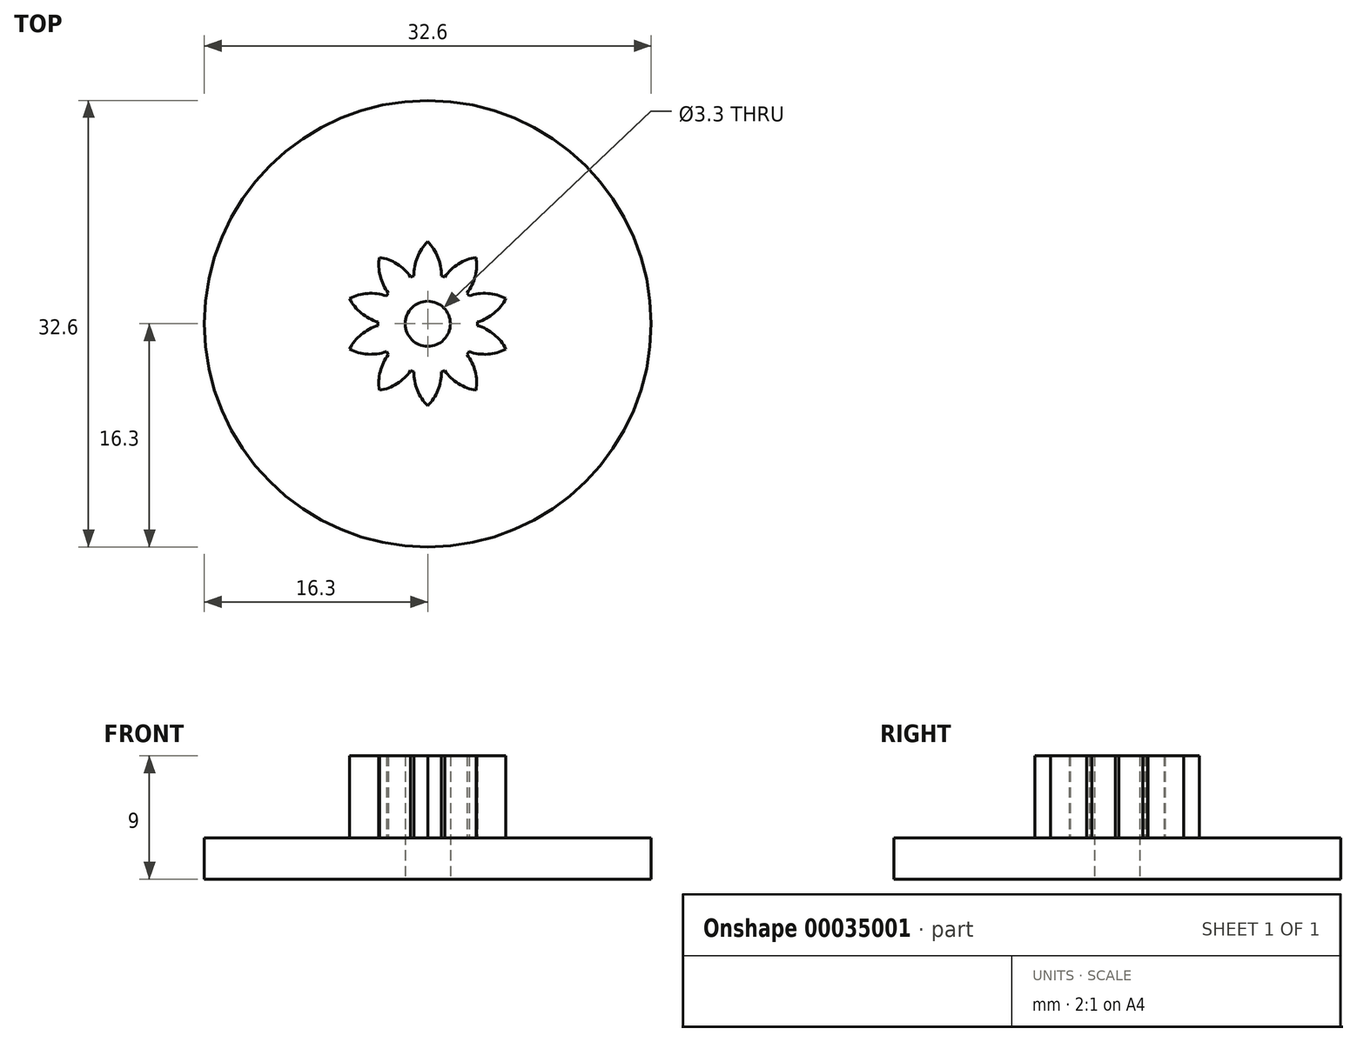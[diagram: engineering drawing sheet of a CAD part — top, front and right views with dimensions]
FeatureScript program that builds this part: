
annotation { "Feature Type Name" : "Feature", "Feature Type Description" : "" }
export const myFeature = defineFeature(function(context is Context, id is Id, definition is map)
    precondition{}
    {
        {
            var Q0;
            Q0=qCreatedBy(makeId("Top.planeOp"),FACE);
            var sketch = newSketch(context, id + "F0", { "sketchPlane" : qUnion([Q0])});
            skArc(sketch, "E0.62.0", {"start": v(9.16, 14.8) * mm, "mid": v(9.2, 14.18) * mm, "end": v(9, 13.59) * mm});
            skArc(sketch, "E0.62.3", {"start": v(9.16, 14.8) * mm, "mid": v(8.6, 14.55) * mm, "end": v(8.15, 14.12) * mm});
            skCircle(sketch, "E1", {"center": v(0, 0) * mm, "radius": 16.3 * mm});
            skPoint(sketch, "E2.center", {"position": v(-0.1, -0.17) * mm});
            skCircle(sketch, "E3", {"center": v(0, 0) * mm, "radius": 1.65 * mm});
            skPoint(sketch, "E4.center", {"position": v(-0.03, -0.04) * mm});
            skPoint(sketch, "E5.center", {"position": v(-0.02, -0.03) * mm});
            skArc(sketch, "E6.1.0", {"start": v(7.74, 15.58) * mm, "mid": v(7.84, 14.97) * mm, "end": v(7.7, 14.37) * mm});
            skArc(sketch, "E6.1.1", {"start": v(7.74, 15.58) * mm, "mid": v(7.2, 15.29) * mm, "end": v(6.8, 14.81) * mm});
            skArc(sketch, "E6.2.0", {"start": v(6.26, 16.23) * mm, "mid": v(6.4, 15.63) * mm, "end": v(6.33, 15.02) * mm});
            skArc(sketch, "E6.2.1", {"start": v(6.26, 16.23) * mm, "mid": v(5.74, 15.89) * mm, "end": v(5.4, 15.38) * mm});
            skArc(sketch, "E6.3.0", {"start": v(4.72, 16.74) * mm, "mid": v(4.93, 16.16) * mm, "end": v(4.9, 15.54) * mm});
            skArc(sketch, "E6.3.1", {"start": v(4.72, 16.74) * mm, "mid": v(4.24, 16.35) * mm, "end": v(3.94, 15.81) * mm});
            skArc(sketch, "E6.4.0", {"start": v(3.14, 17.1) * mm, "mid": v(3.4, 16.55) * mm, "end": v(3.43, 15.93) * mm});
            skArc(sketch, "E6.4.1", {"start": v(3.14, 17.1) * mm, "mid": v(2.7, 16.67) * mm, "end": v(2.45, 16.1) * mm});
            skArc(sketch, "E6.5.0", {"start": v(1.53, 17.32) * mm, "mid": v(1.84, 16.79) * mm, "end": v(1.93, 16.18) * mm});
            skArc(sketch, "E6.5.1", {"start": v(1.53, 17.32) * mm, "mid": v(1.13, 16.85) * mm, "end": v(0.94, 16.26) * mm});
            skArc(sketch, "E6.6.0", {"start": v(-0.09, 17.38) * mm, "mid": v(0.27, 16.88) * mm, "end": v(0.42, 16.28) * mm});
            skArc(sketch, "E6.6.1", {"start": v(-0.09, 17.38) * mm, "mid": v(-0.44, 16.88) * mm, "end": v(-0.58, 16.27) * mm});
            skArc(sketch, "E6.7.0", {"start": v(-1.7, 17.3) * mm, "mid": v(-1.3, 16.83) * mm, "end": v(-1.1, 16.24) * mm});
            skArc(sketch, "E6.7.1", {"start": v(-1.7, 17.3) * mm, "mid": v(-2.01, 16.76) * mm, "end": v(-2.1, 16.14) * mm});
            skArc(sketch, "E6.8.0", {"start": v(-3.31, 17.05) * mm, "mid": v(-2.87, 16.63) * mm, "end": v(-2.6, 16.07) * mm});
            skArc(sketch, "E6.8.1", {"start": v(-3.31, 17.05) * mm, "mid": v(-3.56, 16.49) * mm, "end": v(-3.59, 15.87) * mm});
            skArc(sketch, "E6.9.0", {"start": v(-4.89, 16.66) * mm, "mid": v(-4.4, 16.28) * mm, "end": v(-4.1, 15.75) * mm});
            skArc(sketch, "E6.9.1", {"start": v(-4.89, 16.66) * mm, "mid": v(-5.08, 16.08) * mm, "end": v(-5.05, 15.46) * mm});
            skArc(sketch, "E6.10.0", {"start": v(-6.42, 16.13) * mm, "mid": v(-5.9, 15.8) * mm, "end": v(-5.54, 15.29) * mm});
            skArc(sketch, "E6.10.1", {"start": v(-6.42, 16.13) * mm, "mid": v(-6.56, 15.53) * mm, "end": v(-6.47, 14.91) * mm});
            skArc(sketch, "E6.11.0", {"start": v(-7.9, 15.45) * mm, "mid": v(-7.34, 15.17) * mm, "end": v(-6.94, 14.7) * mm});
            skArc(sketch, "E6.11.1", {"start": v(-7.9, 15.45) * mm, "mid": v(-7.98, 14.84) * mm, "end": v(-7.83, 14.24) * mm});
            skArc(sketch, "E6.12.0", {"start": v(-9.3, 14.64) * mm, "mid": v(-8.72, 14.4) * mm, "end": v(-8.28, 13.98) * mm});
            skArc(sketch, "E6.12.1", {"start": v(-9.3, 14.64) * mm, "mid": v(-9.32, 14.02) * mm, "end": v(-9.12, 13.44) * mm});
            skArc(sketch, "E6.13.0", {"start": v(-10.62, 13.7) * mm, "mid": v(-10.03, 13.52) * mm, "end": v(-9.54, 13.14) * mm});
            skArc(sketch, "E6.13.1", {"start": v(-10.62, 13.7) * mm, "mid": v(-10.59, 13.08) * mm, "end": v(-10.33, 12.52) * mm});
            skArc(sketch, "E6.14.0", {"start": v(-11.85, 12.64) * mm, "mid": v(-11.24, 12.52) * mm, "end": v(-10.72, 12.18) * mm});
            skArc(sketch, "E6.14.1", {"start": v(-11.85, 12.64) * mm, "mid": v(-11.76, 12.03) * mm, "end": v(-11.45, 11.5) * mm});
            skArc(sketch, "E6.15.0", {"start": v(-12.97, 11.47) * mm, "mid": v(-12.35, 11.4) * mm, "end": v(-11.8, 11.12) * mm});
            skArc(sketch, "E6.15.1", {"start": v(-12.97, 11.47) * mm, "mid": v(-12.82, 10.87) * mm, "end": v(-12.47, 10.37) * mm});
            skArc(sketch, "E6.16.0", {"start": v(-13.98, 10.2) * mm, "mid": v(-13.36, 10.2) * mm, "end": v(-12.79, 9.96) * mm});
            skArc(sketch, "E6.16.1", {"start": v(-13.98, 10.2) * mm, "mid": v(-13.78, 9.62) * mm, "end": v(-13.37, 9.15) * mm});
            skArc(sketch, "E6.17.0", {"start": v(-14.86, 8.85) * mm, "mid": v(-14.25, 8.9) * mm, "end": v(-13.66, 8.72) * mm});
            skArc(sketch, "E6.17.1", {"start": v(-14.86, 8.85) * mm, "mid": v(-14.6, 8.28) * mm, "end": v(-14.16, 7.85) * mm});
            skArc(sketch, "E6.18.0", {"start": v(-15.62, 7.41) * mm, "mid": v(-15.01, 7.52) * mm, "end": v(-14.4, 7.4) * mm});
            skArc(sketch, "E6.18.1", {"start": v(-15.62, 7.41) * mm, "mid": v(-15.31, 6.87) * mm, "end": v(-14.83, 6.49) * mm});
            skArc(sketch, "E6.19.0", {"start": v(-16.24, 5.91) * mm, "mid": v(-15.64, 6.08) * mm, "end": v(-15.03, 6) * mm});
            skArc(sketch, "E6.19.1", {"start": v(-16.24, 5.91) * mm, "mid": v(-15.88, 5.4) * mm, "end": v(-15.36, 5.06) * mm});
            skArc(sketch, "E6.20.0", {"start": v(-16.71, 4.36) * mm, "mid": v(-16.13, 4.58) * mm, "end": v(-15.51, 4.57) * mm});
            skArc(sketch, "E6.20.1", {"start": v(-16.71, 4.36) * mm, "mid": v(-16.3, 3.89) * mm, "end": v(-15.76, 3.6) * mm});
            skArc(sketch, "E6.21.0", {"start": v(-17.04, 2.77) * mm, "mid": v(-16.48, 3.04) * mm, "end": v(-15.87, 3.1) * mm});
            skArc(sketch, "E6.21.1", {"start": v(-17.04, 2.77) * mm, "mid": v(-16.6, 2.34) * mm, "end": v(-16.02, 2.1) * mm});
            skArc(sketch, "E6.22.0", {"start": v(-17.21, 1.16) * mm, "mid": v(-16.69, 1.48) * mm, "end": v(-16.08, 1.59) * mm});
            skArc(sketch, "E6.22.1", {"start": v(-17.21, 1.16) * mm, "mid": v(-16.73, 0.77) * mm, "end": v(-16.14, 0.59) * mm});
            skArc(sketch, "E6.23.0", {"start": v(-17.24, -0.46) * mm, "mid": v(-16.74, -0.1) * mm, "end": v(-16.15, 0.07) * mm});
            skArc(sketch, "E6.23.1", {"start": v(-17.24, -0.46) * mm, "mid": v(-16.72, -0.8) * mm, "end": v(-16.12, -0.93) * mm});
            skArc(sketch, "E6.24.0", {"start": v(-17.11, -2.08) * mm, "mid": v(-16.65, -1.66) * mm, "end": v(-16.08, -1.44) * mm});
            skArc(sketch, "E6.24.1", {"start": v(-17.11, -2.08) * mm, "mid": v(-16.56, -2.37) * mm, "end": v(-15.95, -2.44) * mm});
            skArc(sketch, "E6.25.0", {"start": v(-16.83, -3.68) * mm, "mid": v(-16.42, -3.22) * mm, "end": v(-15.86, -2.95) * mm});
            skArc(sketch, "E6.25.1", {"start": v(-16.83, -3.68) * mm, "mid": v(-16.26, -3.91) * mm, "end": v(-15.64, -3.93) * mm});
            skArc(sketch, "E6.26.0", {"start": v(-16.4, -5.24) * mm, "mid": v(-16.03, -4.75) * mm, "end": v(-15.5, -4.42) * mm});
            skArc(sketch, "E6.26.1", {"start": v(-16.4, -5.24) * mm, "mid": v(-15.82, -5.43) * mm, "end": v(-15.2, -5.38) * mm});
            skArc(sketch, "E6.27.0", {"start": v(-15.84, -6.76) * mm, "mid": v(-15.51, -6.23) * mm, "end": v(-15.02, -5.86) * mm});
            skArc(sketch, "E6.27.1", {"start": v(-15.84, -6.76) * mm, "mid": v(-15.23, -6.89) * mm, "end": v(-14.62, -6.78) * mm});
            skArc(sketch, "E6.28.0", {"start": v(-15.13, -8.22) * mm, "mid": v(-14.85, -7.66) * mm, "end": v(-14.4, -7.25) * mm});
            skArc(sketch, "E6.28.1", {"start": v(-15.13, -8.22) * mm, "mid": v(-14.5, -8.29) * mm, "end": v(-13.91, -8.13) * mm});
            skArc(sketch, "E6.29.0", {"start": v(-14.28, -9.6) * mm, "mid": v(-14.06, -9.02) * mm, "end": v(-13.64, -8.57) * mm});
            skArc(sketch, "E6.29.1", {"start": v(-14.28, -9.6) * mm, "mid": v(-13.66, -9.61) * mm, "end": v(-13.08, -9.4) * mm});
            skArc(sketch, "E6.30.0", {"start": v(-13.31, -10.9) * mm, "mid": v(-13.15, -10.3) * mm, "end": v(-12.77, -9.81) * mm});
            skArc(sketch, "E6.30.1", {"start": v(-13.31, -10.9) * mm, "mid": v(-12.7, -10.86) * mm, "end": v(-12.14, -10.59) * mm});
            skArc(sketch, "E6.31.0", {"start": v(-12.22, -12.1) * mm, "mid": v(-12.11, -11.5) * mm, "end": v(-11.79, -10.97) * mm});
            skArc(sketch, "E6.31.1", {"start": v(-12.22, -12.1) * mm, "mid": v(-11.61, -12) * mm, "end": v(-11.08, -11.68) * mm});
            skArc(sketch, "E6.32.0", {"start": v(-11.03, -13.2) * mm, "mid": v(-10.98, -12.58) * mm, "end": v(-10.7, -12.03) * mm});
            skArc(sketch, "E6.32.1", {"start": v(-11.03, -13.2) * mm, "mid": v(-10.43, -13.04) * mm, "end": v(-9.93, -12.67) * mm});
            skArc(sketch, "E6.33.0", {"start": v(-9.74, -14.18) * mm, "mid": v(-9.74, -13.56) * mm, "end": v(-9.52, -12.98) * mm});
            skArc(sketch, "E6.33.1", {"start": v(-9.74, -14.18) * mm, "mid": v(-9.15, -13.96) * mm, "end": v(-8.7, -13.55) * mm});
            skArc(sketch, "E6.34.0", {"start": v(-8.36, -15.03) * mm, "mid": v(-8.42, -14.42) * mm, "end": v(-8.25, -13.82) * mm});
            skArc(sketch, "E6.34.1", {"start": v(-8.36, -15.03) * mm, "mid": v(-7.8, -14.76) * mm, "end": v(-7.38, -14.3) * mm});
            skArc(sketch, "E6.35.0", {"start": v(-6.9, -15.75) * mm, "mid": v(-7.03, -15.15) * mm, "end": v(-6.92, -14.54) * mm});
            skArc(sketch, "E6.35.1", {"start": v(-6.9, -15.75) * mm, "mid": v(-6.37, -15.43) * mm, "end": v(-6, -14.94) * mm});
            skArc(sketch, "E6.36.0", {"start": v(-5.39, -16.34) * mm, "mid": v(-5.57, -15.74) * mm, "end": v(-5.52, -15.13) * mm});
            skArc(sketch, "E6.36.1", {"start": v(-5.39, -16.34) * mm, "mid": v(-4.9, -15.97) * mm, "end": v(-4.56, -15.44) * mm});
            skArc(sketch, "E6.37.0", {"start": v(-3.83, -16.77) * mm, "mid": v(-4.06, -16.2) * mm, "end": v(-4.07, -15.58) * mm});
            skArc(sketch, "E6.37.1", {"start": v(-3.83, -16.77) * mm, "mid": v(-3.37, -16.36) * mm, "end": v(-3.09, -15.8) * mm});
            skArc(sketch, "E6.38.0", {"start": v(-2.23, -17.06) * mm, "mid": v(-2.52, -16.51) * mm, "end": v(-2.58, -15.9) * mm});
            skArc(sketch, "E6.38.1", {"start": v(-2.23, -17.06) * mm, "mid": v(-1.81, -16.6) * mm, "end": v(-1.59, -16.03) * mm});
            skArc(sketch, "E6.39.0", {"start": v(-0.62, -17.2) * mm, "mid": v(-0.95, -16.68) * mm, "end": v(-1.07, -16.08) * mm});
            skArc(sketch, "E6.39.1", {"start": v(-0.62, -17.2) * mm, "mid": v(-0.24, -16.71) * mm, "end": v(-0.07, -16.11) * mm});
            skArc(sketch, "E6.40.0", {"start": v(1, -17.19) * mm, "mid": v(0.62, -16.7) * mm, "end": v(0.44, -16.11) * mm});
            skArc(sketch, "E6.40.1", {"start": v(1, -17.19) * mm, "mid": v(1.33, -16.66) * mm, "end": v(1.45, -16.06) * mm});
            skArc(sketch, "E6.41.0", {"start": v(2.62, -17.02) * mm, "mid": v(2.2, -16.58) * mm, "end": v(1.96, -16) * mm});
            skArc(sketch, "E6.41.1", {"start": v(2.62, -17.02) * mm, "mid": v(2.9, -16.47) * mm, "end": v(2.95, -15.85) * mm});
            skArc(sketch, "E6.42.0", {"start": v(4.2, -16.7) * mm, "mid": v(3.74, -16.3) * mm, "end": v(3.46, -15.75) * mm});
            skArc(sketch, "E6.42.1", {"start": v(4.2, -16.7) * mm, "mid": v(4.43, -16.13) * mm, "end": v(4.43, -15.51) * mm});
            skArc(sketch, "E6.43.0", {"start": v(5.76, -16.25) * mm, "mid": v(5.26, -15.88) * mm, "end": v(4.93, -15.36) * mm});
            skArc(sketch, "E6.43.1", {"start": v(5.76, -16.25) * mm, "mid": v(5.93, -15.65) * mm, "end": v(5.87, -15.03) * mm});
            skArc(sketch, "E6.44.0", {"start": v(7.27, -15.64) * mm, "mid": v(6.73, -15.33) * mm, "end": v(6.35, -14.84) * mm});
            skArc(sketch, "E6.44.1", {"start": v(7.27, -15.64) * mm, "mid": v(7.38, -15.03) * mm, "end": v(7.26, -14.42) * mm});
            skArc(sketch, "E6.45.0", {"start": v(8.7, -14.9) * mm, "mid": v(8.15, -14.63) * mm, "end": v(7.72, -14.19) * mm});
            skArc(sketch, "E6.45.1", {"start": v(8.7, -14.9) * mm, "mid": v(8.76, -14.28) * mm, "end": v(8.59, -13.68) * mm});
            skArc(sketch, "E6.46.0", {"start": v(10.07, -14.02) * mm, "mid": v(9.5, -13.81) * mm, "end": v(9.02, -13.4) * mm});
            skArc(sketch, "E6.46.1", {"start": v(10.07, -14.02) * mm, "mid": v(10.07, -13.4) * mm, "end": v(9.84, -12.82) * mm});
            skArc(sketch, "E6.47.0", {"start": v(11.35, -13.02) * mm, "mid": v(10.75, -12.87) * mm, "end": v(10.25, -12.5) * mm});
            skArc(sketch, "E6.47.1", {"start": v(11.35, -13.02) * mm, "mid": v(11.29, -12.4) * mm, "end": v(11, -11.85) * mm});
            skArc(sketch, "E6.48.0", {"start": v(12.53, -11.9) * mm, "mid": v(11.92, -11.8) * mm, "end": v(11.38, -11.5) * mm});
            skArc(sketch, "E6.48.1", {"start": v(12.53, -11.9) * mm, "mid": v(12.4, -11.3) * mm, "end": v(12.08, -10.77) * mm});
            skArc(sketch, "E6.49.0", {"start": v(13.6, -10.68) * mm, "mid": v(12.98, -10.64) * mm, "end": v(12.42, -10.38) * mm});
            skArc(sketch, "E6.49.1", {"start": v(13.6, -10.68) * mm, "mid": v(13.42, -10.09) * mm, "end": v(13.04, -9.6) * mm});
            skArc(sketch, "E6.50.0", {"start": v(14.54, -9.37) * mm, "mid": v(13.92, -9.39) * mm, "end": v(13.34, -9.18) * mm});
            skArc(sketch, "E6.50.1", {"start": v(14.54, -9.37) * mm, "mid": v(14.31, -8.8) * mm, "end": v(13.89, -8.34) * mm});
            skArc(sketch, "E6.51.0", {"start": v(15.36, -7.97) * mm, "mid": v(14.75, -8.05) * mm, "end": v(14.15, -7.9) * mm});
            skArc(sketch, "E6.51.1", {"start": v(15.36, -7.97) * mm, "mid": v(15.08, -7.42) * mm, "end": v(14.62, -7) * mm});
            skArc(sketch, "E6.52.0", {"start": v(16.05, -6.5) * mm, "mid": v(15.45, -6.63) * mm, "end": v(14.84, -6.54) * mm});
            skArc(sketch, "E6.52.1", {"start": v(16.05, -6.5) * mm, "mid": v(15.72, -5.98) * mm, "end": v(15.22, -5.61) * mm});
            skArc(sketch, "E6.53.0", {"start": v(16.6, -4.97) * mm, "mid": v(16, -5.16) * mm, "end": v(15.4, -5.13) * mm});
            skArc(sketch, "E6.53.1", {"start": v(16.6, -4.97) * mm, "mid": v(16.22, -4.48) * mm, "end": v(15.68, -4.17) * mm});
            skArc(sketch, "E6.54.0", {"start": v(17, -3.4) * mm, "mid": v(16.43, -3.65) * mm, "end": v(15.81, -3.67) * mm});
            skArc(sketch, "E6.54.1", {"start": v(17, -3.4) * mm, "mid": v(16.57, -2.95) * mm, "end": v(16.01, -2.68) * mm});
            skArc(sketch, "E6.55.0", {"start": v(17.25, -1.8) * mm, "mid": v(16.7, -2.1) * mm, "end": v(16.1, -2.17) * mm});
            skArc(sketch, "E6.55.1", {"start": v(17.25, -1.8) * mm, "mid": v(16.79, -1.39) * mm, "end": v(16.2, -1.18) * mm});
            skArc(sketch, "E6.56.0", {"start": v(17.35, -0.18) * mm, "mid": v(16.84, -0.53) * mm, "end": v(16.24, -0.66) * mm});
            skArc(sketch, "E6.56.1", {"start": v(17.35, -0.18) * mm, "mid": v(16.85, 0.19) * mm, "end": v(16.25, 0.34) * mm});
            skArc(sketch, "E6.57.0", {"start": v(17.3, 1.44) * mm, "mid": v(16.82, 1.05) * mm, "end": v(16.23, 0.86) * mm});
            skArc(sketch, "E6.57.1", {"start": v(17.3, 1.44) * mm, "mid": v(16.77, 1.76) * mm, "end": v(16.16, 1.86) * mm});
            skArc(sketch, "E6.58.0", {"start": v(17.1, 3.05) * mm, "mid": v(16.66, 2.61) * mm, "end": v(16.1, 2.37) * mm});
            skArc(sketch, "E6.58.1", {"start": v(17.1, 3.05) * mm, "mid": v(16.54, 3.32) * mm, "end": v(15.92, 3.36) * mm});
            skArc(sketch, "E6.59.0", {"start": v(16.74, 4.63) * mm, "mid": v(16.35, 4.16) * mm, "end": v(15.8, 3.86) * mm});
            skArc(sketch, "E6.59.1", {"start": v(16.74, 4.63) * mm, "mid": v(16.16, 4.85) * mm, "end": v(15.54, 4.83) * mm});
            skArc(sketch, "E6.60.0", {"start": v(16.24, 6.18) * mm, "mid": v(15.9, 5.67) * mm, "end": v(15.38, 5.32) * mm});
            skArc(sketch, "E6.60.1", {"start": v(16.24, 6.18) * mm, "mid": v(15.65, 6.33) * mm, "end": v(15.03, 6.26) * mm});
            skArc(sketch, "E6.61.0", {"start": v(15.6, 7.67) * mm, "mid": v(15.3, 7.13) * mm, "end": v(14.83, 6.73) * mm});
            skArc(sketch, "E6.61.1", {"start": v(15.6, 7.67) * mm, "mid": v(15, 7.77) * mm, "end": v(14.39, 7.63) * mm});
            skArc(sketch, "E6.62.0", {"start": v(14.82, 9.09) * mm, "mid": v(14.58, 8.52) * mm, "end": v(14.14, 8.09) * mm});
            skArc(sketch, "E6.62.1", {"start": v(14.82, 9.09) * mm, "mid": v(14.2, 9.13) * mm, "end": v(13.62, 8.94) * mm});
            skArc(sketch, "E6.63.0", {"start": v(13.92, 10.43) * mm, "mid": v(13.72, 9.85) * mm, "end": v(13.33, 9.37) * mm});
            skArc(sketch, "E6.63.1", {"start": v(13.92, 10.43) * mm, "mid": v(13.3, 10.42) * mm, "end": v(12.73, 10.17) * mm});
            skArc(sketch, "E6.64.0", {"start": v(12.89, 11.69) * mm, "mid": v(12.75, 11.08) * mm, "end": v(12.4, 10.57) * mm});
            skArc(sketch, "E6.64.1", {"start": v(12.89, 11.69) * mm, "mid": v(12.27, 11.61) * mm, "end": v(11.73, 11.32) * mm});
            skArc(sketch, "E6.65.0", {"start": v(11.74, 12.84) * mm, "mid": v(11.66, 12.22) * mm, "end": v(11.36, 11.68) * mm});
            skArc(sketch, "E6.65.1", {"start": v(11.74, 12.84) * mm, "mid": v(11.14, 12.7) * mm, "end": v(10.62, 12.36) * mm});
            skArc(sketch, "E6.66.0", {"start": v(10.5, 13.88) * mm, "mid": v(10.48, 13.26) * mm, "end": v(10.23, 12.7) * mm});
            skArc(sketch, "E6.66.1", {"start": v(10.5, 13.88) * mm, "mid": v(9.9, 13.69) * mm, "end": v(9.43, 13.3) * mm});
            skPoint(sketch, "E6.center", {"position": v(0.05, 0.09) * mm});
            skSolve(sketch);
        }
        {
            var Q0;
            {var subQ0=sQuery(id+"F0.wireOp",EDGE,"E0.62.0");Q0=makeQuery(id+"F0.imprint","IMPRINT",FACE,{"disambiguationData":[TD([[makeQuery(id+"F0.imprint","IMPRINT",EDGE,{"derivedFrom":subQ0}),-1.0]])]});}
            var Q1;
            Q1=makeQuery(id+"F0.imprint","IMPRINT",FACE,{"disambiguationData":[TD([[makeQuery(id+"F0.imprint","IMPRINT",EDGE,{"derivedFrom":sQuery(id+"F0.wireOp",EDGE,"E3")}),-1.0]])]});
            var Q2;
            {var subQ0=sQuery(id+"F0.wireOp",EDGE,"E6.16.0");Q2=makeQuery(id+"F0.imprint","IMPRINT",FACE,{"disambiguationData":[TD([[makeQuery(id+"F0.imprint","IMPRINT",EDGE,{"derivedFrom":subQ0}),-1.0]])]});}
            var Q3;
            {var subQ0=sQuery(id+"F0.wireOp",EDGE,"E6.27.0");Q3=makeQuery(id+"F0.imprint","IMPRINT",FACE,{"disambiguationData":[TD([[makeQuery(id+"F0.imprint","IMPRINT",EDGE,{"derivedFrom":subQ0}),-1.0]])]});}
            var Q4;
            {var subQ0=sQuery(id+"F0.wireOp",EDGE,"E6.20.0");Q4=makeQuery(id+"F0.imprint","IMPRINT",FACE,{"disambiguationData":[TD([[makeQuery(id+"F0.imprint","IMPRINT",EDGE,{"derivedFrom":subQ0}),-1.0]])]});}
            var Q5;
            {var subQ0=sQuery(id+"F0.wireOp",EDGE,"E6.32.0");Q5=makeQuery(id+"F0.imprint","IMPRINT",FACE,{"disambiguationData":[TD([[makeQuery(id+"F0.imprint","IMPRINT",EDGE,{"derivedFrom":subQ0}),-1.0]])]});}
            var Q6;
            {var subQ0=sQuery(id+"F0.wireOp",EDGE,"E6.15.0");Q6=makeQuery(id+"F0.imprint","IMPRINT",FACE,{"disambiguationData":[TD([[makeQuery(id+"F0.imprint","IMPRINT",EDGE,{"derivedFrom":subQ0}),-1.0]])]});}
            var Q7;
            {var subQ0=sQuery(id+"F0.wireOp",EDGE,"E6.12.0");Q7=makeQuery(id+"F0.imprint","IMPRINT",FACE,{"disambiguationData":[TD([[makeQuery(id+"F0.imprint","IMPRINT",EDGE,{"derivedFrom":subQ0}),-1.0]])]});}
            var Q8;
            {var subQ0=sQuery(id+"F0.wireOp",EDGE,"E6.25.0");Q8=makeQuery(id+"F0.imprint","IMPRINT",FACE,{"disambiguationData":[TD([[makeQuery(id+"F0.imprint","IMPRINT",EDGE,{"derivedFrom":subQ0}),-1.0]])]});}
            var Q9;
            {var subQ0=sQuery(id+"F0.wireOp",EDGE,"E6.14.0");Q9=makeQuery(id+"F0.imprint","IMPRINT",FACE,{"disambiguationData":[TD([[makeQuery(id+"F0.imprint","IMPRINT",EDGE,{"derivedFrom":subQ0}),-1.0]])]});}
            var Q10;
            {var subQ0=sQuery(id+"F0.wireOp",EDGE,"E6.35.0");Q10=makeQuery(id+"F0.imprint","IMPRINT",FACE,{"disambiguationData":[TD([[makeQuery(id+"F0.imprint","IMPRINT",EDGE,{"derivedFrom":subQ0}),-1.0]])]});}
            var Q11;
            {var subQ0=sQuery(id+"F0.wireOp",EDGE,"E6.19.0");Q11=makeQuery(id+"F0.imprint","IMPRINT",FACE,{"disambiguationData":[TD([[makeQuery(id+"F0.imprint","IMPRINT",EDGE,{"derivedFrom":subQ0}),-1.0]])]});}
            var Q12;
            {var subQ0=sQuery(id+"F0.wireOp",EDGE,"E6.26.0");Q12=makeQuery(id+"F0.imprint","IMPRINT",FACE,{"disambiguationData":[TD([[makeQuery(id+"F0.imprint","IMPRINT",EDGE,{"derivedFrom":subQ0}),-1.0]])]});}
            var Q13;
            {var subQ0=sQuery(id+"F0.wireOp",EDGE,"E6.28.0");Q13=makeQuery(id+"F0.imprint","IMPRINT",FACE,{"disambiguationData":[TD([[makeQuery(id+"F0.imprint","IMPRINT",EDGE,{"derivedFrom":subQ0}),-1.0]])]});}
            var Q14;
            {var subQ0=sQuery(id+"F0.wireOp",EDGE,"E6.17.0");Q14=makeQuery(id+"F0.imprint","IMPRINT",FACE,{"disambiguationData":[TD([[makeQuery(id+"F0.imprint","IMPRINT",EDGE,{"derivedFrom":subQ0}),-1.0]])]});}
            var Q15;
            {var subQ0=sQuery(id+"F0.wireOp",EDGE,"E6.11.0");Q15=makeQuery(id+"F0.imprint","IMPRINT",FACE,{"disambiguationData":[TD([[makeQuery(id+"F0.imprint","IMPRINT",EDGE,{"derivedFrom":subQ0}),-1.0]])]});}
            var Q16;
            {var subQ0=sQuery(id+"F0.wireOp",EDGE,"E6.30.0");Q16=makeQuery(id+"F0.imprint","IMPRINT",FACE,{"disambiguationData":[TD([[makeQuery(id+"F0.imprint","IMPRINT",EDGE,{"derivedFrom":subQ0}),-1.0]])]});}
            var Q17;
            {var subQ0=sQuery(id+"F0.wireOp",EDGE,"E6.18.0");Q17=makeQuery(id+"F0.imprint","IMPRINT",FACE,{"disambiguationData":[TD([[makeQuery(id+"F0.imprint","IMPRINT",EDGE,{"derivedFrom":subQ0}),-1.0]])]});}
            var Q18;
            {var subQ0=sQuery(id+"F0.wireOp",EDGE,"E6.34.0");Q18=makeQuery(id+"F0.imprint","IMPRINT",FACE,{"disambiguationData":[TD([[makeQuery(id+"F0.imprint","IMPRINT",EDGE,{"derivedFrom":subQ0}),-1.0]])]});}
            var Q19;
            {var subQ0=sQuery(id+"F0.wireOp",EDGE,"E6.24.0");Q19=makeQuery(id+"F0.imprint","IMPRINT",FACE,{"disambiguationData":[TD([[makeQuery(id+"F0.imprint","IMPRINT",EDGE,{"derivedFrom":subQ0}),-1.0]])]});}
            var Q20;
            {var subQ0=sQuery(id+"F0.wireOp",EDGE,"E6.21.0");Q20=makeQuery(id+"F0.imprint","IMPRINT",FACE,{"disambiguationData":[TD([[makeQuery(id+"F0.imprint","IMPRINT",EDGE,{"derivedFrom":subQ0}),-1.0]])]});}
            var Q21;
            {var subQ0=sQuery(id+"F0.wireOp",EDGE,"E6.10.0");Q21=makeQuery(id+"F0.imprint","IMPRINT",FACE,{"disambiguationData":[TD([[makeQuery(id+"F0.imprint","IMPRINT",EDGE,{"derivedFrom":subQ0}),-1.0]])]});}
            var Q22;
            {var subQ0=sQuery(id+"F0.wireOp",EDGE,"E6.31.0");Q22=makeQuery(id+"F0.imprint","IMPRINT",FACE,{"disambiguationData":[TD([[makeQuery(id+"F0.imprint","IMPRINT",EDGE,{"derivedFrom":subQ0}),-1.0]])]});}
            var Q23;
            {var subQ0=sQuery(id+"F0.wireOp",EDGE,"E6.22.0");Q23=makeQuery(id+"F0.imprint","IMPRINT",FACE,{"disambiguationData":[TD([[makeQuery(id+"F0.imprint","IMPRINT",EDGE,{"derivedFrom":subQ0}),-1.0]])]});}
            var Q24;
            {var subQ0=sQuery(id+"F0.wireOp",EDGE,"E6.23.0");Q24=makeQuery(id+"F0.imprint","IMPRINT",FACE,{"disambiguationData":[TD([[makeQuery(id+"F0.imprint","IMPRINT",EDGE,{"derivedFrom":subQ0}),-1.0]])]});}
            var Q25;
            {var subQ0=sQuery(id+"F0.wireOp",EDGE,"E6.33.0");Q25=makeQuery(id+"F0.imprint","IMPRINT",FACE,{"disambiguationData":[TD([[makeQuery(id+"F0.imprint","IMPRINT",EDGE,{"derivedFrom":subQ0}),-1.0]])]});}
            var Q26;
            {var subQ0=sQuery(id+"F0.wireOp",EDGE,"E6.29.0");Q26=makeQuery(id+"F0.imprint","IMPRINT",FACE,{"disambiguationData":[TD([[makeQuery(id+"F0.imprint","IMPRINT",EDGE,{"derivedFrom":subQ0}),-1.0]])]});}
            var Q27;
            {var subQ0=sQuery(id+"F0.wireOp",EDGE,"E6.43.0");Q27=makeQuery(id+"F0.imprint","IMPRINT",FACE,{"disambiguationData":[TD([[makeQuery(id+"F0.imprint","IMPRINT",EDGE,{"derivedFrom":subQ0}),-1.0]])]});}
            var Q28;
            {var subQ0=sQuery(id+"F0.wireOp",EDGE,"E6.45.0");Q28=makeQuery(id+"F0.imprint","IMPRINT",FACE,{"disambiguationData":[TD([[makeQuery(id+"F0.imprint","IMPRINT",EDGE,{"derivedFrom":subQ0}),-1.0]])]});}
            var Q29;
            {var subQ0=sQuery(id+"F0.wireOp",EDGE,"E6.49.0");Q29=makeQuery(id+"F0.imprint","IMPRINT",FACE,{"disambiguationData":[TD([[makeQuery(id+"F0.imprint","IMPRINT",EDGE,{"derivedFrom":subQ0}),-1.0]])]});}
            var Q30;
            {var subQ0=sQuery(id+"F0.wireOp",EDGE,"E6.37.0");Q30=makeQuery(id+"F0.imprint","IMPRINT",FACE,{"disambiguationData":[TD([[makeQuery(id+"F0.imprint","IMPRINT",EDGE,{"derivedFrom":subQ0}),-1.0]])]});}
            var Q31;
            {var subQ0=sQuery(id+"F0.wireOp",EDGE,"E6.48.0");Q31=makeQuery(id+"F0.imprint","IMPRINT",FACE,{"disambiguationData":[TD([[makeQuery(id+"F0.imprint","IMPRINT",EDGE,{"derivedFrom":subQ0}),-1.0]])]});}
            var Q32;
            {var subQ0=sQuery(id+"F0.wireOp",EDGE,"E6.53.0");Q32=makeQuery(id+"F0.imprint","IMPRINT",FACE,{"disambiguationData":[TD([[makeQuery(id+"F0.imprint","IMPRINT",EDGE,{"derivedFrom":subQ0}),-1.0]])]});}
            var Q33;
            {var subQ0=sQuery(id+"F0.wireOp",EDGE,"E6.39.0");Q33=makeQuery(id+"F0.imprint","IMPRINT",FACE,{"disambiguationData":[TD([[makeQuery(id+"F0.imprint","IMPRINT",EDGE,{"derivedFrom":subQ0}),-1.0]])]});}
            var Q34;
            {var subQ0=sQuery(id+"F0.wireOp",EDGE,"E6.51.0");Q34=makeQuery(id+"F0.imprint","IMPRINT",FACE,{"disambiguationData":[TD([[makeQuery(id+"F0.imprint","IMPRINT",EDGE,{"derivedFrom":subQ0}),-1.0]])]});}
            var Q35;
            {var subQ0=sQuery(id+"F0.wireOp",EDGE,"E6.46.0");Q35=makeQuery(id+"F0.imprint","IMPRINT",FACE,{"disambiguationData":[TD([[makeQuery(id+"F0.imprint","IMPRINT",EDGE,{"derivedFrom":subQ0}),-1.0]])]});}
            var Q36;
            {var subQ0=sQuery(id+"F0.wireOp",EDGE,"E6.40.0");Q36=makeQuery(id+"F0.imprint","IMPRINT",FACE,{"disambiguationData":[TD([[makeQuery(id+"F0.imprint","IMPRINT",EDGE,{"derivedFrom":subQ0}),-1.0]])]});}
            var Q37;
            {var subQ0=sQuery(id+"F0.wireOp",EDGE,"E6.50.0");Q37=makeQuery(id+"F0.imprint","IMPRINT",FACE,{"disambiguationData":[TD([[makeQuery(id+"F0.imprint","IMPRINT",EDGE,{"derivedFrom":subQ0}),-1.0]])]});}
            var Q38;
            {var subQ0=sQuery(id+"F0.wireOp",EDGE,"E6.36.0");Q38=makeQuery(id+"F0.imprint","IMPRINT",FACE,{"disambiguationData":[TD([[makeQuery(id+"F0.imprint","IMPRINT",EDGE,{"derivedFrom":subQ0}),-1.0]])]});}
            var Q39;
            {var subQ0=sQuery(id+"F0.wireOp",EDGE,"E6.47.0");Q39=makeQuery(id+"F0.imprint","IMPRINT",FACE,{"disambiguationData":[TD([[makeQuery(id+"F0.imprint","IMPRINT",EDGE,{"derivedFrom":subQ0}),-1.0]])]});}
            var Q40;
            {var subQ0=sQuery(id+"F0.wireOp",EDGE,"E6.41.0");Q40=makeQuery(id+"F0.imprint","IMPRINT",FACE,{"disambiguationData":[TD([[makeQuery(id+"F0.imprint","IMPRINT",EDGE,{"derivedFrom":subQ0}),-1.0]])]});}
            var Q41;
            {var subQ0=sQuery(id+"F0.wireOp",EDGE,"E6.52.0");Q41=makeQuery(id+"F0.imprint","IMPRINT",FACE,{"disambiguationData":[TD([[makeQuery(id+"F0.imprint","IMPRINT",EDGE,{"derivedFrom":subQ0}),-1.0]])]});}
            var Q42;
            {var subQ0=sQuery(id+"F0.wireOp",EDGE,"E6.44.0");Q42=makeQuery(id+"F0.imprint","IMPRINT",FACE,{"disambiguationData":[TD([[makeQuery(id+"F0.imprint","IMPRINT",EDGE,{"derivedFrom":subQ0}),-1.0]])]});}
            var Q43;
            {var subQ0=sQuery(id+"F0.wireOp",EDGE,"E6.38.0");Q43=makeQuery(id+"F0.imprint","IMPRINT",FACE,{"disambiguationData":[TD([[makeQuery(id+"F0.imprint","IMPRINT",EDGE,{"derivedFrom":subQ0}),-1.0]])]});}
            var Q44;
            {var subQ0=sQuery(id+"F0.wireOp",EDGE,"E6.42.0");Q44=makeQuery(id+"F0.imprint","IMPRINT",FACE,{"disambiguationData":[TD([[makeQuery(id+"F0.imprint","IMPRINT",EDGE,{"derivedFrom":subQ0}),-1.0]])]});}
            var Q45;
            {var subQ0=sQuery(id+"F0.wireOp",EDGE,"E6.63.0");Q45=makeQuery(id+"F0.imprint","IMPRINT",FACE,{"disambiguationData":[TD([[makeQuery(id+"F0.imprint","IMPRINT",EDGE,{"derivedFrom":subQ0}),-1.0]])]});}
            var Q46;
            {var subQ0=sQuery(id+"F0.wireOp",EDGE,"E6.62.0");Q46=makeQuery(id+"F0.imprint","IMPRINT",FACE,{"disambiguationData":[TD([[makeQuery(id+"F0.imprint","IMPRINT",EDGE,{"derivedFrom":subQ0}),-1.0]])]});}
            var Q47;
            {var subQ0=sQuery(id+"F0.wireOp",EDGE,"E6.60.0");Q47=makeQuery(id+"F0.imprint","IMPRINT",FACE,{"disambiguationData":[TD([[makeQuery(id+"F0.imprint","IMPRINT",EDGE,{"derivedFrom":subQ0}),-1.0]])]});}
            var Q48;
            {var subQ0=sQuery(id+"F0.wireOp",EDGE,"E6.55.0");Q48=makeQuery(id+"F0.imprint","IMPRINT",FACE,{"disambiguationData":[TD([[makeQuery(id+"F0.imprint","IMPRINT",EDGE,{"derivedFrom":subQ0}),-1.0]])]});}
            var Q49;
            {var subQ0=sQuery(id+"F0.wireOp",EDGE,"E6.65.0");Q49=makeQuery(id+"F0.imprint","IMPRINT",FACE,{"disambiguationData":[TD([[makeQuery(id+"F0.imprint","IMPRINT",EDGE,{"derivedFrom":subQ0}),-1.0]])]});}
            var Q50;
            {var subQ0=sQuery(id+"F0.wireOp",EDGE,"E6.64.0");Q50=makeQuery(id+"F0.imprint","IMPRINT",FACE,{"disambiguationData":[TD([[makeQuery(id+"F0.imprint","IMPRINT",EDGE,{"derivedFrom":subQ0}),-1.0]])]});}
            var Q51;
            {var subQ0=sQuery(id+"F0.wireOp",EDGE,"E6.54.0");Q51=makeQuery(id+"F0.imprint","IMPRINT",FACE,{"disambiguationData":[TD([[makeQuery(id+"F0.imprint","IMPRINT",EDGE,{"derivedFrom":subQ0}),-1.0]])]});}
            var Q52;
            {var subQ0=sQuery(id+"F0.wireOp",EDGE,"E6.56.0");Q52=makeQuery(id+"F0.imprint","IMPRINT",FACE,{"disambiguationData":[TD([[makeQuery(id+"F0.imprint","IMPRINT",EDGE,{"derivedFrom":subQ0}),-1.0]])]});}
            var Q53;
            {var subQ0=sQuery(id+"F0.wireOp",EDGE,"E6.66.0");Q53=makeQuery(id+"F0.imprint","IMPRINT",FACE,{"disambiguationData":[TD([[makeQuery(id+"F0.imprint","IMPRINT",EDGE,{"derivedFrom":subQ0}),-1.0]])]});}
            var Q54;
            {var subQ0=sQuery(id+"F0.wireOp",EDGE,"E6.61.0");Q54=makeQuery(id+"F0.imprint","IMPRINT",FACE,{"disambiguationData":[TD([[makeQuery(id+"F0.imprint","IMPRINT",EDGE,{"derivedFrom":subQ0}),-1.0]])]});}
            var Q55;
            {var subQ0=sQuery(id+"F0.wireOp",EDGE,"E6.59.0");Q55=makeQuery(id+"F0.imprint","IMPRINT",FACE,{"disambiguationData":[TD([[makeQuery(id+"F0.imprint","IMPRINT",EDGE,{"derivedFrom":subQ0}),-1.0]])]});}
            var Q56;
            {var subQ0=sQuery(id+"F0.wireOp",EDGE,"E6.58.0");Q56=makeQuery(id+"F0.imprint","IMPRINT",FACE,{"disambiguationData":[TD([[makeQuery(id+"F0.imprint","IMPRINT",EDGE,{"derivedFrom":subQ0}),-1.0]])]});}
            var Q57;
            {var subQ0=sQuery(id+"F0.wireOp",EDGE,"E6.57.0");Q57=makeQuery(id+"F0.imprint","IMPRINT",FACE,{"disambiguationData":[TD([[makeQuery(id+"F0.imprint","IMPRINT",EDGE,{"derivedFrom":subQ0}),-1.0]])]});}
            var Q58;
            {var subQ0=sQuery(id+"F0.wireOp",EDGE,"E6.1.0");Q58=makeQuery(id+"F0.imprint","IMPRINT",FACE,{"disambiguationData":[TD([[makeQuery(id+"F0.imprint","IMPRINT",EDGE,{"derivedFrom":subQ0}),-1.0]])]});}
            var Q59;
            {var subQ0=sQuery(id+"F0.wireOp",EDGE,"E6.8.0");Q59=makeQuery(id+"F0.imprint","IMPRINT",FACE,{"disambiguationData":[TD([[makeQuery(id+"F0.imprint","IMPRINT",EDGE,{"derivedFrom":subQ0}),-1.0]])]});}
            var Q60;
            {var subQ0=sQuery(id+"F0.wireOp",EDGE,"E6.3.0");Q60=makeQuery(id+"F0.imprint","IMPRINT",FACE,{"disambiguationData":[TD([[makeQuery(id+"F0.imprint","IMPRINT",EDGE,{"derivedFrom":subQ0}),-1.0]])]});}
            var Q61;
            {var subQ0=sQuery(id+"F0.wireOp",EDGE,"E6.2.0");Q61=makeQuery(id+"F0.imprint","IMPRINT",FACE,{"disambiguationData":[TD([[makeQuery(id+"F0.imprint","IMPRINT",EDGE,{"derivedFrom":subQ0}),-1.0]])]});}
            var Q62;
            {var subQ0=sQuery(id+"F0.wireOp",EDGE,"E6.9.0");Q62=makeQuery(id+"F0.imprint","IMPRINT",FACE,{"disambiguationData":[TD([[makeQuery(id+"F0.imprint","IMPRINT",EDGE,{"derivedFrom":subQ0}),-1.0]])]});}
            var Q63;
            {var subQ0=sQuery(id+"F0.wireOp",EDGE,"E6.5.0");Q63=makeQuery(id+"F0.imprint","IMPRINT",FACE,{"disambiguationData":[TD([[makeQuery(id+"F0.imprint","IMPRINT",EDGE,{"derivedFrom":subQ0}),-1.0]])]});}
            var Q64;
            {var subQ0=sQuery(id+"F0.wireOp",EDGE,"E6.6.0");Q64=makeQuery(id+"F0.imprint","IMPRINT",FACE,{"disambiguationData":[TD([[makeQuery(id+"F0.imprint","IMPRINT",EDGE,{"derivedFrom":subQ0}),-1.0]])]});}
            var Q65;
            {var subQ0=sQuery(id+"F0.wireOp",EDGE,"E6.7.0");Q65=makeQuery(id+"F0.imprint","IMPRINT",FACE,{"disambiguationData":[TD([[makeQuery(id+"F0.imprint","IMPRINT",EDGE,{"derivedFrom":subQ0}),-1.0]])]});}
            var Q66;
            {var subQ0=sQuery(id+"F0.wireOp",EDGE,"E6.4.0");Q66=makeQuery(id+"F0.imprint","IMPRINT",FACE,{"disambiguationData":[TD([[makeQuery(id+"F0.imprint","IMPRINT",EDGE,{"derivedFrom":subQ0}),-1.0]])]});}
            var Q67;
            {var subQ0=sQuery(id+"F0.wireOp",EDGE,"E6.13.0");Q67=makeQuery(id+"F0.imprint","IMPRINT",FACE,{"disambiguationData":[TD([[makeQuery(id+"F0.imprint","IMPRINT",EDGE,{"derivedFrom":subQ0}),-1.0]])]});}
            extrude(context, id + "F1", {"entities" : qUnion([Q0, Q1, Q2, Q3, Q4, Q5, Q6, Q7, Q8, Q9, Q10, Q11, Q12, Q13, Q14, Q15, Q16, Q17, Q18, Q19, Q20, Q21, Q22, Q23, Q24, Q25, Q26, Q27, Q28, Q29, Q30, Q31, Q32, Q33, Q34, Q35, Q36, Q37, Q38, Q39, Q40, Q41, Q42, Q43, Q44, Q45, Q46, Q47, Q48, Q49, Q50, Q51, Q52, Q53, Q54, Q55, Q56, Q57, Q58, Q59, Q60, Q61, Q62, Q63, Q64, Q65, Q66, Q67]), "depth" : 3 * mm});
        }
        {
            var Q0;
            Q0=makeQuery(id+"F1.opExtrude","CAP_FACE",FACE,{"disambiguationData":[OSD([sQuery(id+"F0.wireOp",EDGE,"qGQ1WXnv-DlxU-2AYN-OX4b-y1Stcrvec96w"),sQuery(id+"F0.wireOp",EDGE,"4It7DnyK-UarK-GTSr-ItDN-6rkJHOTMADGP"),sQuery(id+"F0.wireOp",EDGE,"474310cc-bcfc-40c8-8a0e-4de7f26ed0060.MirrorCS"),sQuery(id+"F0.wireOp",EDGE,"E0.1.0"),sQuery(id+"F0.wireOp",EDGE,"E0.1.3"),sQuery(id+"F0.wireOp",EDGE,"E0.2.0"),sQuery(id+"F0.wireOp",EDGE,"E0.2.3"),sQuery(id+"F0.wireOp",EDGE,"E0.3.0"),sQuery(id+"F0.wireOp",EDGE,"E0.3.3"),sQuery(id+"F0.wireOp",EDGE,"E0.4.0"),sQuery(id+"F0.wireOp",EDGE,"E0.4.3"),sQuery(id+"F0.wireOp",EDGE,"E0.5.0"),sQuery(id+"F0.wireOp",EDGE,"E0.5.3"),sQuery(id+"F0.wireOp",EDGE,"E0.6.0"),sQuery(id+"F0.wireOp",EDGE,"E0.6.3"),sQuery(id+"F0.wireOp",EDGE,"E0.7.0"),sQuery(id+"F0.wireOp",EDGE,"E0.7.3"),sQuery(id+"F0.wireOp",EDGE,"E0.8.0"),sQuery(id+"F0.wireOp",EDGE,"E0.8.3"),sQuery(id+"F0.wireOp",EDGE,"E0.9.0"),sQuery(id+"F0.wireOp",EDGE,"E0.9.3"),sQuery(id+"F0.wireOp",EDGE,"E0.10.0"),sQuery(id+"F0.wireOp",EDGE,"E0.10.3"),sQuery(id+"F0.wireOp",EDGE,"E0.11.0"),sQuery(id+"F0.wireOp",EDGE,"E0.11.3"),sQuery(id+"F0.wireOp",EDGE,"E0.12.0"),sQuery(id+"F0.wireOp",EDGE,"E0.12.3"),sQuery(id+"F0.wireOp",EDGE,"E0.13.0"),sQuery(id+"F0.wireOp",EDGE,"E0.13.3"),sQuery(id+"F0.wireOp",EDGE,"E0.14.0"),sQuery(id+"F0.wireOp",EDGE,"E0.14.3"),sQuery(id+"F0.wireOp",EDGE,"E0.15.0"),sQuery(id+"F0.wireOp",EDGE,"E0.15.3"),sQuery(id+"F0.wireOp",EDGE,"E0.16.0"),sQuery(id+"F0.wireOp",EDGE,"E0.16.3"),sQuery(id+"F0.wireOp",EDGE,"E0.17.0"),sQuery(id+"F0.wireOp",EDGE,"E0.17.3"),sQuery(id+"F0.wireOp",EDGE,"E0.18.0"),sQuery(id+"F0.wireOp",EDGE,"E0.18.3"),sQuery(id+"F0.wireOp",EDGE,"E0.19.0"),sQuery(id+"F0.wireOp",EDGE,"E0.19.3"),sQuery(id+"F0.wireOp",EDGE,"E0.20.0"),sQuery(id+"F0.wireOp",EDGE,"E0.20.3"),sQuery(id+"F0.wireOp",EDGE,"E0.21.0"),sQuery(id+"F0.wireOp",EDGE,"E0.21.3"),sQuery(id+"F0.wireOp",EDGE,"E0.22.0"),sQuery(id+"F0.wireOp",EDGE,"E0.22.3"),sQuery(id+"F0.wireOp",EDGE,"E0.23.0"),sQuery(id+"F0.wireOp",EDGE,"E0.23.3"),sQuery(id+"F0.wireOp",EDGE,"E0.24.0"),sQuery(id+"F0.wireOp",EDGE,"E0.24.3"),sQuery(id+"F0.wireOp",EDGE,"E0.25.0"),sQuery(id+"F0.wireOp",EDGE,"E0.25.3"),sQuery(id+"F0.wireOp",EDGE,"E0.26.0"),sQuery(id+"F0.wireOp",EDGE,"E0.26.3"),sQuery(id+"F0.wireOp",EDGE,"E0.27.0"),sQuery(id+"F0.wireOp",EDGE,"E0.27.3"),sQuery(id+"F0.wireOp",EDGE,"E0.28.0"),sQuery(id+"F0.wireOp",EDGE,"E0.28.3"),sQuery(id+"F0.wireOp",EDGE,"E0.29.0"),sQuery(id+"F0.wireOp",EDGE,"E0.29.3"),sQuery(id+"F0.wireOp",EDGE,"E0.30.0"),sQuery(id+"F0.wireOp",EDGE,"E0.30.3"),sQuery(id+"F0.wireOp",EDGE,"E0.31.0"),sQuery(id+"F0.wireOp",EDGE,"E0.31.3"),sQuery(id+"F0.wireOp",EDGE,"E0.32.0"),sQuery(id+"F0.wireOp",EDGE,"E0.32.3"),sQuery(id+"F0.wireOp",EDGE,"E0.33.0"),sQuery(id+"F0.wireOp",EDGE,"E0.33.3"),sQuery(id+"F0.wireOp",EDGE,"E0.34.0"),sQuery(id+"F0.wireOp",EDGE,"E0.34.3"),sQuery(id+"F0.wireOp",EDGE,"E0.35.0"),sQuery(id+"F0.wireOp",EDGE,"E0.35.3"),sQuery(id+"F0.wireOp",EDGE,"E0.36.0"),sQuery(id+"F0.wireOp",EDGE,"E0.36.3"),sQuery(id+"F0.wireOp",EDGE,"E0.37.0"),sQuery(id+"F0.wireOp",EDGE,"E0.37.3"),sQuery(id+"F0.wireOp",EDGE,"E0.38.0"),sQuery(id+"F0.wireOp",EDGE,"E0.38.3"),sQuery(id+"F0.wireOp",EDGE,"E0.39.0"),sQuery(id+"F0.wireOp",EDGE,"E0.39.3"),sQuery(id+"F0.wireOp",EDGE,"E0.40.0"),sQuery(id+"F0.wireOp",EDGE,"E0.40.3"),sQuery(id+"F0.wireOp",EDGE,"E0.41.0"),sQuery(id+"F0.wireOp",EDGE,"E0.41.3"),sQuery(id+"F0.wireOp",EDGE,"E0.42.0"),sQuery(id+"F0.wireOp",EDGE,"E0.42.3"),sQuery(id+"F0.wireOp",EDGE,"E0.43.0"),sQuery(id+"F0.wireOp",EDGE,"E0.43.3"),sQuery(id+"F0.wireOp",EDGE,"E0.44.0"),sQuery(id+"F0.wireOp",EDGE,"E0.44.3"),sQuery(id+"F0.wireOp",EDGE,"E0.45.0"),sQuery(id+"F0.wireOp",EDGE,"E0.45.3"),sQuery(id+"F0.wireOp",EDGE,"E0.46.0"),sQuery(id+"F0.wireOp",EDGE,"E0.46.3"),sQuery(id+"F0.wireOp",EDGE,"E0.47.0"),sQuery(id+"F0.wireOp",EDGE,"E0.47.3"),sQuery(id+"F0.wireOp",EDGE,"E0.48.0"),sQuery(id+"F0.wireOp",EDGE,"E0.48.3"),sQuery(id+"F0.wireOp",EDGE,"E0.49.0"),sQuery(id+"F0.wireOp",EDGE,"E0.49.3"),sQuery(id+"F0.wireOp",EDGE,"E0.50.0"),sQuery(id+"F0.wireOp",EDGE,"E0.50.3"),sQuery(id+"F0.wireOp",EDGE,"E0.51.0"),sQuery(id+"F0.wireOp",EDGE,"E0.51.3"),sQuery(id+"F0.wireOp",EDGE,"E0.52.0"),sQuery(id+"F0.wireOp",EDGE,"E0.52.3"),sQuery(id+"F0.wireOp",EDGE,"E0.53.0"),sQuery(id+"F0.wireOp",EDGE,"E0.53.3"),sQuery(id+"F0.wireOp",EDGE,"E0.54.0"),sQuery(id+"F0.wireOp",EDGE,"E0.54.3"),sQuery(id+"F0.wireOp",EDGE,"E0.55.0"),sQuery(id+"F0.wireOp",EDGE,"E0.55.3"),sQuery(id+"F0.wireOp",EDGE,"E0.56.0"),sQuery(id+"F0.wireOp",EDGE,"E0.56.3"),sQuery(id+"F0.wireOp",EDGE,"E0.57.0"),sQuery(id+"F0.wireOp",EDGE,"E0.57.3"),sQuery(id+"F0.wireOp",EDGE,"E0.58.0"),sQuery(id+"F0.wireOp",EDGE,"E0.58.3"),sQuery(id+"F0.wireOp",EDGE,"E0.59.0"),sQuery(id+"F0.wireOp",EDGE,"E0.59.3"),sQuery(id+"F0.wireOp",EDGE,"E0.60.0"),sQuery(id+"F0.wireOp",EDGE,"E0.60.3"),sQuery(id+"F0.wireOp",EDGE,"E0.61.0"),sQuery(id+"F0.wireOp",EDGE,"E0.61.3"),sQuery(id+"F0.wireOp",EDGE,"E0.62.0"),sQuery(id+"F0.wireOp",EDGE,"E0.62.3"),sQuery(id+"F0.wireOp",EDGE,"E0.63.0"),sQuery(id+"F0.wireOp",EDGE,"E0.63.3"),sQuery(id+"F0.wireOp",EDGE,"E0.64.0"),sQuery(id+"F0.wireOp",EDGE,"E0.64.3"),sQuery(id+"F0.wireOp",EDGE,"E0.65.0"),sQuery(id+"F0.wireOp",EDGE,"E0.65.3"),sQuery(id+"F0.wireOp",EDGE,"E0.66.0"),sQuery(id+"F0.wireOp",EDGE,"E0.66.3"),sQuery(id+"F0.wireOp",EDGE,"E0.67.0"),sQuery(id+"F0.wireOp",EDGE,"E0.67.3"),sQuery(id+"F0.wireOp",EDGE,"E1")])],"isStart":false});
            var sketch = newSketch(context, id + "F2", { "sketchPlane" : qUnion([Q0])});
            skLineSegment(sketch, "E7", {"start": v(0, 6) * mm, "end": v(0, 3.5) * mm, "construction": true});
            skLineSegment(sketch, "E8", {"start": v(0, 3.5) * mm, "end": v(-1, 3.5) * mm, "construction": true});
            skArc(sketch, "E9", {"start": v(0, 6) * mm, "mid": v(-0.76, 4.85) * mm, "end": v(-1, 3.5) * mm});
            skArc(sketch, "E10.MirrorCS", {"start": v(0, 6) * mm, "mid": v(0.76, 4.85) * mm, "end": v(1, 3.5) * mm});
            skArc(sketch, "E11.1.0", {"start": v(-3.53, 4.85) * mm, "mid": v(-2.24, 4.37) * mm, "end": v(-1.25, 3.42) * mm});
            skArc(sketch, "E11.1.1", {"start": v(-3.53, 4.85) * mm, "mid": v(-3.46, 3.48) * mm, "end": v(-2.87, 2.24) * mm});
            skArc(sketch, "E11.2.0", {"start": v(-5.7, 1.85) * mm, "mid": v(-4.38, 2.22) * mm, "end": v(-3.02, 2.03) * mm});
            skArc(sketch, "E11.2.1", {"start": v(-5.7, 1.85) * mm, "mid": v(-4.85, 0.78) * mm, "end": v(-3.64, 0.13) * mm});
            skArc(sketch, "E11.3.0", {"start": v(-5.7, -1.85) * mm, "mid": v(-4.85, -0.78) * mm, "end": v(-3.64, -0.13) * mm});
            skArc(sketch, "E11.3.1", {"start": v(-5.7, -1.85) * mm, "mid": v(-4.38, -2.22) * mm, "end": v(-3.02, -2.03) * mm});
            skArc(sketch, "E11.4.0", {"start": v(-3.53, -4.85) * mm, "mid": v(-3.46, -3.48) * mm, "end": v(-2.87, -2.24) * mm});
            skArc(sketch, "E11.4.1", {"start": v(-3.53, -4.85) * mm, "mid": v(-2.24, -4.37) * mm, "end": v(-1.25, -3.42) * mm});
            skArc(sketch, "E11.5.0", {"start": v(0, -6) * mm, "mid": v(-0.76, -4.85) * mm, "end": v(-1, -3.5) * mm});
            skArc(sketch, "E11.5.1", {"start": v(0, -6) * mm, "mid": v(0.76, -4.85) * mm, "end": v(1, -3.5) * mm});
            skArc(sketch, "E11.6.0", {"start": v(3.53, -4.85) * mm, "mid": v(2.24, -4.37) * mm, "end": v(1.25, -3.42) * mm});
            skArc(sketch, "E11.6.1", {"start": v(3.53, -4.85) * mm, "mid": v(3.46, -3.48) * mm, "end": v(2.87, -2.24) * mm});
            skArc(sketch, "E11.7.0", {"start": v(5.7, -1.85) * mm, "mid": v(4.38, -2.22) * mm, "end": v(3.02, -2.03) * mm});
            skArc(sketch, "E11.7.1", {"start": v(5.7, -1.85) * mm, "mid": v(4.85, -0.78) * mm, "end": v(3.64, -0.13) * mm});
            skArc(sketch, "E11.8.0", {"start": v(5.7, 1.85) * mm, "mid": v(4.85, 0.78) * mm, "end": v(3.64, 0.13) * mm});
            skArc(sketch, "E11.8.1", {"start": v(5.7, 1.85) * mm, "mid": v(4.38, 2.22) * mm, "end": v(3.02, 2.03) * mm});
            skArc(sketch, "E11.9.0", {"start": v(3.53, 4.85) * mm, "mid": v(3.46, 3.48) * mm, "end": v(2.87, 2.24) * mm});
            skArc(sketch, "E11.9.1", {"start": v(3.53, 4.85) * mm, "mid": v(2.24, 4.37) * mm, "end": v(1.25, 3.42) * mm});
            skPoint(sketch, "E11.center", {"position": v(0, 0) * mm});
            skLineSegment(sketch, "E12", {"start": v(1, 3.5) * mm, "end": v(1.25, 3.42) * mm});
            skLineSegment(sketch, "E13", {"start": v(2.87, 2.24) * mm, "end": v(3.02, 2.03) * mm});
            skLineSegment(sketch, "E14", {"start": v(-1, 3.5) * mm, "end": v(-1.25, 3.42) * mm});
            skLineSegment(sketch, "E15", {"start": v(-2.87, 2.24) * mm, "end": v(-3.02, 2.03) * mm});
            skLineSegment(sketch, "E16", {"start": v(3.64, 0.13) * mm, "end": v(3.64, -0.13) * mm});
            skLineSegment(sketch, "E17", {"start": v(3.02, -2.03) * mm, "end": v(2.87, -2.24) * mm});
            skLineSegment(sketch, "E18", {"start": v(1.25, -3.42) * mm, "end": v(1, -3.5) * mm});
            skLineSegment(sketch, "E19", {"start": v(-1, -3.5) * mm, "end": v(-1.25, -3.42) * mm});
            skLineSegment(sketch, "E20", {"start": v(-2.87, -2.24) * mm, "end": v(-3.02, -2.03) * mm});
            skLineSegment(sketch, "E21", {"start": v(-3.64, -0.13) * mm, "end": v(-3.64, 0.13) * mm});
            skSolve(sketch);
        }
        {
            var Q0;
            Q0=makeQuery(id+"F2.imprint","IMPRINT",FACE,{"disambiguationData":[TD([[makeQuery(id+"F2.imprint","IMPRINT",EDGE,{"derivedFrom":sQuery(id+"F2.wireOp",EDGE,"E9")}),1.0]])]});
            extrude(context, id + "F3", {"entities" : qUnion([Q0]), "operationType" : NewBodyOperationType.ADD, "depth" : 6 * mm});
        }
    });
